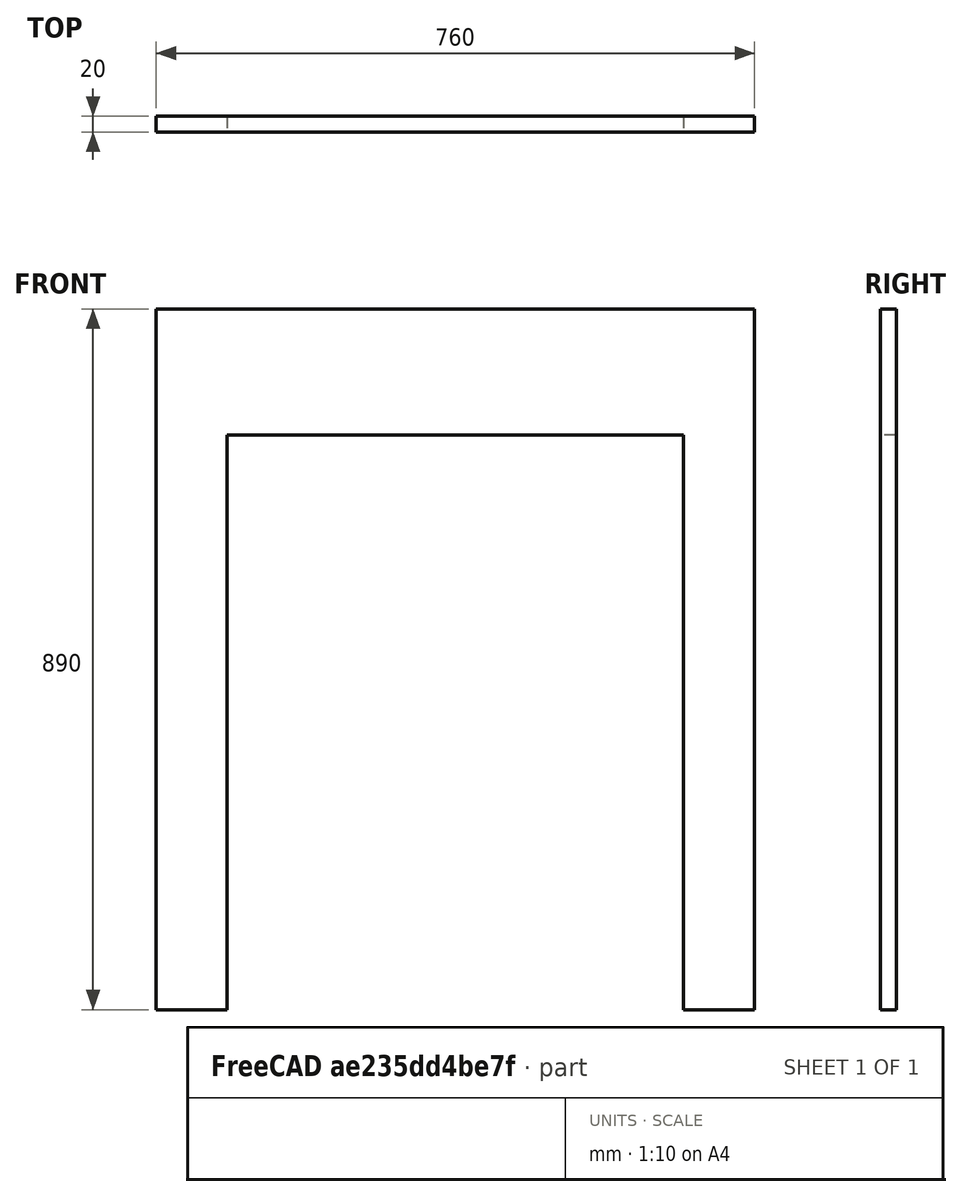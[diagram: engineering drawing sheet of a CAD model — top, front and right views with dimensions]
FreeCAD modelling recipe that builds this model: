
FCSTD DOCUMENT  (FreeCAD 0.20R29603 (Git))
Label: Trennwand
License: All rights reserved
LicenseURL: http://en.wikipedia.org/wiki/All_rights_reserved
objects: Sketcher::SketchObject×1, PartDesign::Pad×1, PartDesign::Body×1
note: 4 computed .brp shape members not serialized (recipe doc carries the construction recipe); baked Part::Feature solids carry a one-line shape summary decoded from their .brp

FEATURE [Sketcher::SketchObject] Sketch
  FullyConstrained = true
  MapMode = 5
  Placement = pos=(0,0,0) rot=(1,0,0;1.5708rad)
  Support = -> [XZ_Plane]
  sketch-geometry (8):
    g0: LineSegment StartX=-380 StartY=0 StartZ=0 EndX=-290 EndY=0 EndZ=0
    g1: LineSegment StartX=-290 StartY=0 StartZ=0 EndX=-290 EndY=730 EndZ=0
    g2: LineSegment StartX=-290 StartY=730 StartZ=0 EndX=290 EndY=730 EndZ=0
    g3: LineSegment StartX=290 StartY=730 StartZ=0 EndX=290 EndY=0 EndZ=0
    g4: LineSegment StartX=290 StartY=0 StartZ=0 EndX=380 EndY=0 EndZ=0
    g5: LineSegment StartX=380 StartY=0 StartZ=0 EndX=380 EndY=890 EndZ=0
    g6: LineSegment StartX=380 StartY=890 StartZ=0 EndX=-380 EndY=890 EndZ=0
    g7: LineSegment StartX=-380 StartY=890 StartZ=0 EndX=-380 EndY=0 EndZ=0
  constraints (22):
    c: Horizontal(g0)
    c: Coincident(g0,g1)
    c: Vertical(g1)
    c: Coincident(g1,g2)
    c: Horizontal(g2)
    c: Coincident(g2,g3)
    c: Vertical(g3)
    c: Coincident(g3,g4)
    c: Coincident(g4,g5)
    c: Vertical(g5)
    c: Coincident(g5,g6)
    c: Horizontal(g6)
    c: Coincident(g6,g7)
    c: Coincident(g7,g0)
    c: Vertical(g7)
    c: PointOnObject(g0,g-1)
    c: Symmetric(g0,g3,g-2)
    c: Symmetric(g0,g4,g-2)
    c: Distance(g6) = 760
    c: Distance(g2) = 580
    c: Distance(g5) = 890
    c: Distance(g5,g2) = 160
FEATURE [PartDesign::Pad] Pad
  Direction = (0,-1,-2e-16)
  Length = 20
  Length2 = 10
  Placement = pos=(0,0,0) rot=(1,0,0;1.5708rad)
  Profile = -> Sketch
  ReferenceAxis = -> Sketch [N_Axis]
  Type = 0
FEATURE [PartDesign::Body] Body
  Group = -> [Sketch,Pad]
  Origin = -> Origin
  Tip = -> Pad
